# Revit family: KingswayGroup_PshPlts_Anti-LigaturePushPlate
name_source: partatom
category: Specialty Equipment
units: mm (PartAtom-declared; Revit-internal decimal feet)

## family parameters
Always vertical = Yes
Cut with Voids When Loaded = No
Part Type = Normal
Room Calculation Point = No
Round Connector Dimension = Use Diameter
Shared = No
Work Plane-Based = No

## types (1)
- KingswayGroup_PshPlts_Anti-LigaturePushPlate
    AssetType = Fixed
    BIMObjectName = KingswayGroup_PushPlates_Anti-LigaturePushPlate
    Category = Pr_30_36_33_68:Push plates
    Color = For full range of available finishes and colours, contact Kingsway Group
    Default Elevation = 0 mm  [stored 0 ft]
    Description = Radiused End Push Plate
    DurationUnit = year
    Features = Manufactured from 3mm solid stainless-steel, the KG100 is a highly-durable, anti-ligature push plate that protects doors from wear
    Finish = For full range of available finishes and colours, contact Kingsway Group
    IfcExportAs = IfcDiscreteAccessoryType
    IfcExportType = USERDEFINED
    Manufacturer = Kingsway Group
    ManufacturerName = Kingsway Group
    ManufacturerURL = https://kingswaygroupglobal.com
    Material = Stainless Steel
    Model = KG100
    ModelNumber = KG100
    ModelReference = Anti-Ligature Push Plate
    Name = PushPlates_Anti-LigaturePushPlate_KG100_KingswayGroup
    NominalHeight = 290 mm  [stored 0.951444 ft]
    NominalLength = 100 mm  [stored 0.328084 ft]
    NominalWidth = 3 mm  [stored 0.00984252 ft]
    PlateMaterial = NBS_Concept
    ProductInformation = https://kingswaygroupglobal.com
    Size = 100 x 290 x 3 mm
    URL = https://kingswaygroupglobal.com
    Uniclass2015Code = Pr_30_36_33_68
    Uniclass2015Title = Push plates
    Uniclass2015Version = Products v1.36
    Version = 1
    WarrantyDescription = 5-Year Guarantee *For faulty manufacture and not for damage
    WarrantyDurationParts = 5
    WarrantyDurationUnit = year

note: [stored X ft] marks values corroborated as IEEE doubles in the binary element streams (Revit-internal decimal feet)

## geometry (parser evidence)
native form markers: Sweep x3
no freeform markers — native parametric forms only
